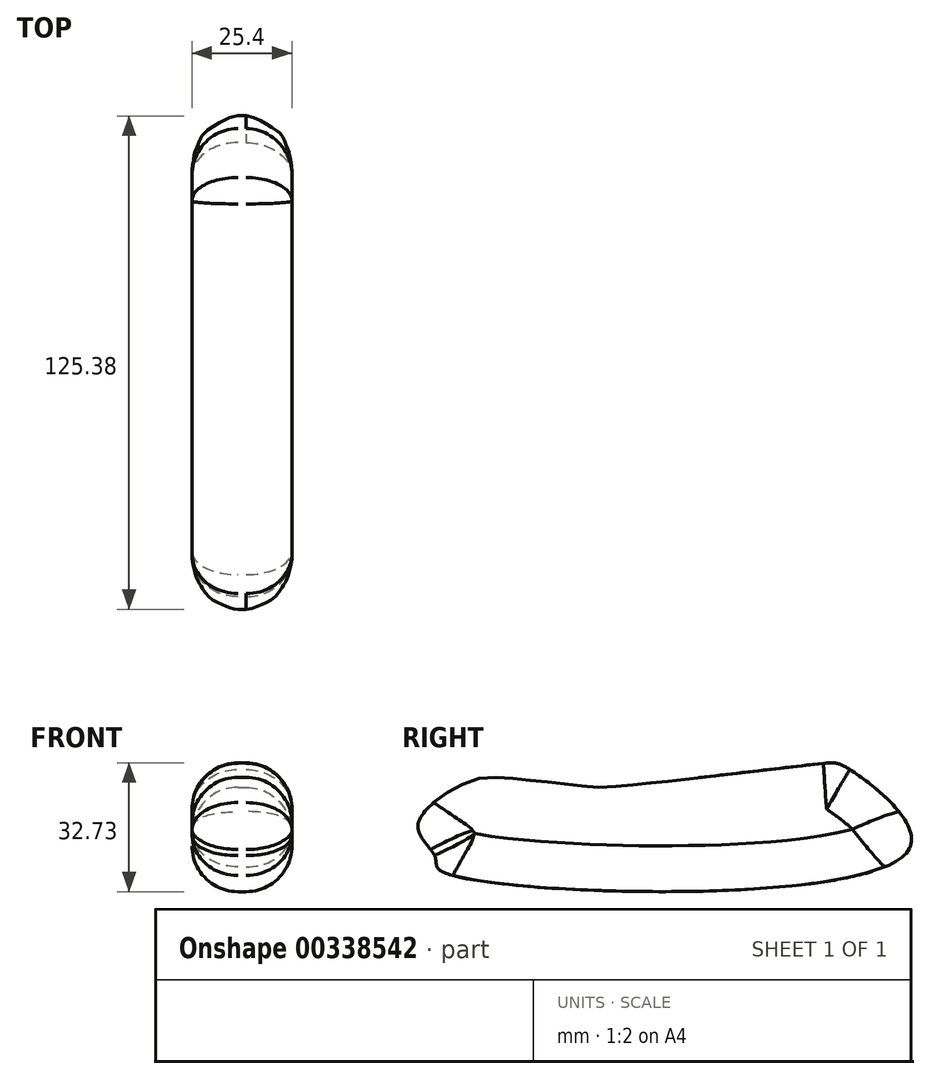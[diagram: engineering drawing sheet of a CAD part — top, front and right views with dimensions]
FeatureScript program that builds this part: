
annotation { "Feature Type Name" : "Feature", "Feature Type Description" : "" }
export const myFeature = defineFeature(function(context is Context, id is Id, definition is map)
    precondition{}
    {
        {
            var Q0;
            Q0=qCreatedBy(makeId("Right.planeOp"),FACE);
            var sketch = newSketch(context, id + "F0", { "sketchPlane" : qUnion([Q0])});
            skFitSpline(sketch, "E0", {"points": [v(-57.7, 15.78) * mm, v(-46.26, 26.4) * mm, v(-36.74, 28.03) * mm, v(-15.24, 25.85) * mm, v(-6.53, 25.85) * mm, v(44.36, 31.57) * mm, v(52.25, 29.94) * mm, v(66.67, 9.25) * mm, v(-51.44, 4.08) * mm, v(-53.34, 7.9) * mm, v(-57.7, 15.78) * mm]});
            skSolve(sketch);
        }
        {
            var Q0;
            Q0 = qSketchRegion(id + "F0", true);
            extrude(context, id + "F1", {"entities" : qUnion([Q0]), "depth" : 25.4 * mm});
        }
        {
            var Q0;
            Q0=makeQuery(id+"F1.opExtrude","CAP_FACE",FACE,{"disambiguationData":[OSD([sQuery(id+"F0.wireOp",EDGE,"E0")])],"isStart":false});
            var Q1;
            Q1=makeQuery(id+"F1.opExtrude","CAP_FACE",FACE,{"disambiguationData":[OSD([sQuery(id+"F0.wireOp",EDGE,"E0")])],"isStart":true});
            fillet(context, id + "F2", {"entities" : qUnion([Q0, Q1]), "radius" : 11.65 * mm, "tangentPropagation" : true, "allowEdgeOverflow" : false});
        }
    });
